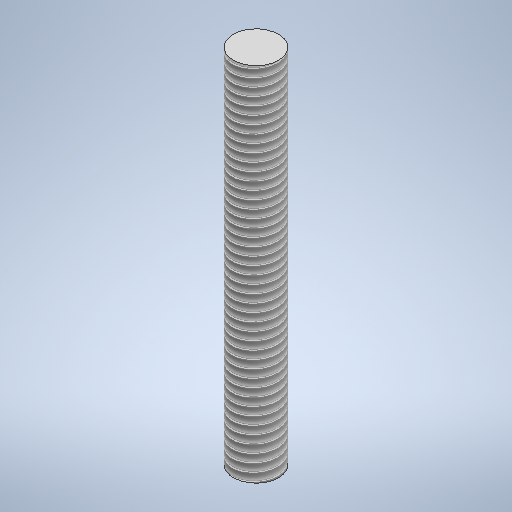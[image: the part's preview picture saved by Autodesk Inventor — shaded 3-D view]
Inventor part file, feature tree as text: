
AUTODESK INVENTOR PART (.ipt)
format: ipt  version: 2025.1 (Build 291241000, 241)  size: 294,400 bytes
history: native  units: mm
features: extrude x1, thread x1, sketch x1
ambient origin geometry x8: Origin, YZ Plane, XZ Plane, XY Plane, X Axis, Y Axis, Z Axis, Center Point
bodies: Solid1 (feature_tree)
feature tree (3):
  extrude  "Extrusion1"  Depth=20.0mm TaperAngle=0.0deg
  thread  "Thread1"  [1 undecoded]
  sketch  "Sketch1"  dims[d0=2.5mm d1=20.0mm d2=0.0mm d3=35.9mm d4=0.0mm]
note: 1 required parameter value undecoded (feature->parameter linkage not recoverable at this tier; creation-order binding heuristic only, values carry confidence <= 0.55)
